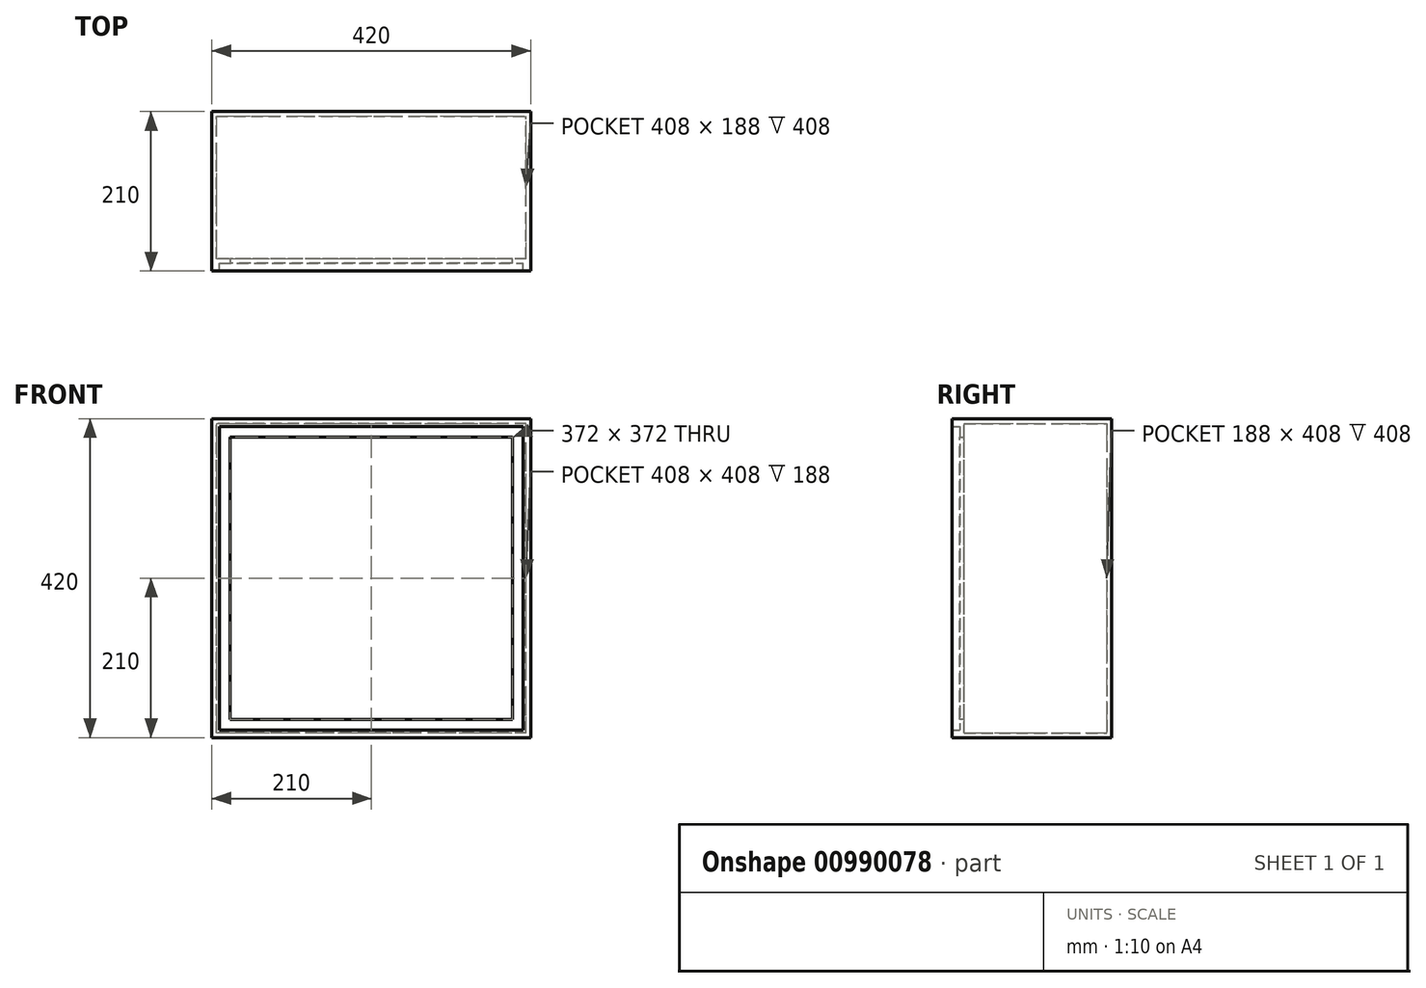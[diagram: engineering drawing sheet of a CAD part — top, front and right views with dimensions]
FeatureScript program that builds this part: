
annotation { "Feature Type Name" : "Feature", "Feature Type Description" : "" }
export const myFeature = defineFeature(function(context is Context, id is Id, definition is map)
    precondition{}
    {
        {
            var Q0;
            Q0=qCreatedBy(makeId("Front.planeOp"),FACE);
            var sketch = newSketch(context, id + "F0", { "sketchPlane" : qUnion([Q0])});
            skLineSegment(sketch, "E0.bottom", {"start": v(-210, 210) * mm, "end": v(210, 210) * mm});
            skLineSegment(sketch, "E0.top", {"start": v(-210, -210) * mm, "end": v(210, -210) * mm});
            skLineSegment(sketch, "E0.left", {"start": v(-210, 210) * mm, "end": v(-210, -210) * mm});
            skLineSegment(sketch, "E0.right", {"start": v(210, 210) * mm, "end": v(210, -210) * mm});
            skPoint(sketch, "E0.middle", {"position": v(0, 0) * mm});
            skSolve(sketch);
        }
        {
            var Q0;
            Q0=qSketchRegion(id+"F0",true);
            extrude(context, id + "F1", {"entities" : qUnion([Q0]), "endBound" : BoundingType.SYMMETRIC, "depth" : 210 * mm, "offsetDistance" : 25.4 * mm});
        }
        {
            var Q0;
            Q0=makeQuery(id+"F1.opExtrude","CAP_FACE",FACE,{"disambiguationData":[OSD([sQuery(id+"F0.wireOp",EDGE,"E0.bottom"),sQuery(id+"F0.wireOp",EDGE,"E0.top"),sQuery(id+"F0.wireOp",EDGE,"E0.left"),sQuery(id+"F0.wireOp",EDGE,"E0.right")])],"isStart":false});
            shell(context, id + "F2", {"entities" : qUnion([Q0]), "thickness" : 6 * mm});
        }
        {
            var Q0;
            Q0=makeQuery(id+"F2.opShell","OFFSET_FACE",FACE,{"disambiguationData":[OSD([sQuery(id+"F0.wireOp",EDGE,"E0.left")])]});
            var sketch = newSketch(context, id + "F3", { "sketchPlane" : qUnion([Q0])});
            skLineSegment(sketch, "E1.top", {"start": v(-2, -194) * mm, "end": v(2, -194) * mm});
            skPoint(sketch, "E1.middle", {"position": v(0, 0) * mm});
            skLineSegment(sketch, "E2.bottom", {"start": v(-89, -204) * mm, "end": v(-95, -204) * mm});
            skLineSegment(sketch, "E2.top", {"start": v(-89, 204) * mm, "end": v(-95, 204) * mm});
            skLineSegment(sketch, "E2.left", {"start": v(-89, -204) * mm, "end": v(-89, 204) * mm});
            skLineSegment(sketch, "E2.right", {"start": v(-95, -204) * mm, "end": v(-95, 204) * mm});
            skPoint(sketch, "E2.middle", {"position": v(-92, 0) * mm});
            skSolve(sketch);
        }
        {
            var Q0;
            Q0=qSketchRegion(id+"F3",true);
            extrude(context, id + "F4", {"entities" : qUnion([Q0]), "operationType" : NewBodyOperationType.ADD, "depth" : 18 * mm, "offsetDistance" : 25.4 * mm});
        }
        {
            var Q0;
            Q0=makeQuery(id+"F2.opShell","OFFSET_FACE",FACE,{"disambiguationData":[OSD([sQuery(id+"F0.wireOp",EDGE,"E0.right")])]});
            var sketch = newSketch(context, id + "F5", { "sketchPlane" : qUnion([Q0])});
            skLineSegment(sketch, "E3.bottom", {"start": v(95, -204) * mm, "end": v(89, -204) * mm});
            skLineSegment(sketch, "E3.top", {"start": v(95, 204) * mm, "end": v(89, 204) * mm});
            skLineSegment(sketch, "E3.left", {"start": v(89, -204) * mm, "end": v(89, 204) * mm});
            skLineSegment(sketch, "E3.right", {"start": v(95, -204) * mm, "end": v(95, 204) * mm});
            skPoint(sketch, "E3.middle", {"position": v(92, 0) * mm});
            skSolve(sketch);
        }
        {
            var Q0;
            Q0=qSketchRegion(id+"F5",true);
            extrude(context, id + "F6", {"entities" : qUnion([Q0]), "operationType" : NewBodyOperationType.ADD, "depth" : 18 * mm, "offsetDistance" : 25.4 * mm});
        }
        {
            var Q0;
            Q0=makeQuery(id+"F4.opExtrude","CAP_FACE",FACE,{"disambiguationData":[OSD([sQuery(id+"F3.wireOp",EDGE,"E2.bottom"),sQuery(id+"F3.wireOp",EDGE,"E2.top"),sQuery(id+"F3.wireOp",EDGE,"E2.left"),sQuery(id+"F3.wireOp",EDGE,"E2.right")])],"isStart":false});
            var sketch = newSketch(context, id + "F7", { "sketchPlane" : qUnion([Q0])});
            skLineSegment(sketch, "E4.bottom", {"start": v(-95, 204) * mm, "end": v(-89, 204) * mm});
            skLineSegment(sketch, "E4.top", {"start": v(-95, 186) * mm, "end": v(-89, 186) * mm});
            skLineSegment(sketch, "E4.left", {"start": v(-95, 204) * mm, "end": v(-95, 186) * mm});
            skLineSegment(sketch, "E4.right", {"start": v(-89, 204) * mm, "end": v(-89, 186) * mm});
            skSolve(sketch);
        }
        {
            var Q0;
            Q0=qSketchRegion(id+"F7",true);
            var Q1;
            Q1=makeQuery(id+"F6.opExtrude","CAP_FACE",FACE,{"disambiguationData":[OSD([sQuery(id+"F5.wireOp",EDGE,"E3.bottom"),sQuery(id+"F5.wireOp",EDGE,"E3.top"),sQuery(id+"F5.wireOp",EDGE,"E3.left"),sQuery(id+"F5.wireOp",EDGE,"E3.right")])],"isStart":false});
            extrude(context, id + "F8", {"entities" : qUnion([Q0]), "operationType" : NewBodyOperationType.ADD, "endBound" : BoundingType.UP_TO_SURFACE, "depth" : 12.2 * mm, "endBoundEntityFace" : qUnion([Q1]), "offsetDistance" : 25.4 * mm});
        }
        {
            var Q0;
            Q0=makeQuery(id+"F4.opExtrude","CAP_FACE",FACE,{"disambiguationData":[OSD([sQuery(id+"F3.wireOp",EDGE,"E2.bottom"),sQuery(id+"F3.wireOp",EDGE,"E2.top"),sQuery(id+"F3.wireOp",EDGE,"E2.left"),sQuery(id+"F3.wireOp",EDGE,"E2.right")])],"isStart":false});
            var sketch = newSketch(context, id + "F9", { "sketchPlane" : qUnion([Q0])});
            skLineSegment(sketch, "E5.bottom", {"start": v(-89, -204) * mm, "end": v(-95, -204) * mm});
            skLineSegment(sketch, "E5.top", {"start": v(-89, -186) * mm, "end": v(-95, -186) * mm});
            skLineSegment(sketch, "E5.left", {"start": v(-89, -204) * mm, "end": v(-89, -186) * mm});
            skLineSegment(sketch, "E5.right", {"start": v(-95, -204) * mm, "end": v(-95, -186) * mm});
            skSolve(sketch);
        }
        {
            var Q0;
            Q0=qSketchRegion(id+"F9",true);
            var Q1;
            Q1=makeQuery(id+"F6.opExtrude","CAP_FACE",FACE,{"disambiguationData":[OSD([sQuery(id+"F5.wireOp",EDGE,"E3.bottom"),sQuery(id+"F5.wireOp",EDGE,"E3.top"),sQuery(id+"F5.wireOp",EDGE,"E3.left"),sQuery(id+"F5.wireOp",EDGE,"E3.right")])],"isStart":false});
            extrude(context, id + "F10", {"entities" : qUnion([Q0]), "operationType" : NewBodyOperationType.ADD, "endBound" : BoundingType.UP_TO_SURFACE, "depth" : 25.4 * mm, "endBoundEntityFace" : qUnion([Q1]), "offsetDistance" : 25.4 * mm});
        }
        {
            var Q0;
            Q0=makeQuery(id+"F10.boolean.opBoolean","MERGE",FACE,{"derivedFrom":[makeQuery(id+"F8.boolean.opBoolean","MERGE",FACE,{"derivedFrom":[makeQuery(id+"F4.opExtrude","SWEPT_FACE",FACE,{"disambiguationData":[OSD([sQuery(id+"F3.wireOp",EDGE,"E2.right")])]}),makeQuery(id+"F6.opExtrude","SWEPT_FACE",FACE,{"disambiguationData":[OSD([sQuery(id+"F5.wireOp",EDGE,"E3.right")])]}),makeQuery(id+"F8.opExtrude","SWEPT_FACE",FACE,{"disambiguationData":[OSD([sQuery(id+"F7.wireOp",EDGE,"E4.left")])]})]}),makeQuery(id+"F10.opExtrude","SWEPT_FACE",FACE,{"disambiguationData":[OSD([sQuery(id+"F9.wireOp",EDGE,"E5.right")])]})]});
            var sketch = newSketch(context, id + "F11", { "sketchPlane" : qUnion([Q0])});
            skLineSegment(sketch, "E6.bottom", {"start": v(-204, 204) * mm, "end": v(204, 204) * mm});
            skLineSegment(sketch, "E6.top", {"start": v(-204, -204) * mm, "end": v(204, -204) * mm});
            skLineSegment(sketch, "E6.left", {"start": v(-204, 204) * mm, "end": v(-204, -204) * mm});
            skLineSegment(sketch, "E6.right", {"start": v(204, 204) * mm, "end": v(204, -204) * mm});
            skPoint(sketch, "E6.middle", {"position": v(0, 0) * mm});
            skLineSegment(sketch, "E7.bottom", {"start": v(-200, 200) * mm, "end": v(200, 200) * mm});
            skLineSegment(sketch, "E7.top", {"start": v(-200, -200) * mm, "end": v(200, -200) * mm});
            skLineSegment(sketch, "E7.left", {"start": v(-200, 200) * mm, "end": v(-200, -200) * mm});
            skLineSegment(sketch, "E7.right", {"start": v(200, 200) * mm, "end": v(200, -200) * mm});
            skSolve(sketch);
        }
        {
            var Q0;
            Q0=qSketchRegion(id+"F11",true);
            extrude(context, id + "F12", {"entities" : qUnion([Q0]), "operationType" : NewBodyOperationType.ADD, "depth" : 10 * mm, "offsetDistance" : 25.4 * mm});
        }
    });
